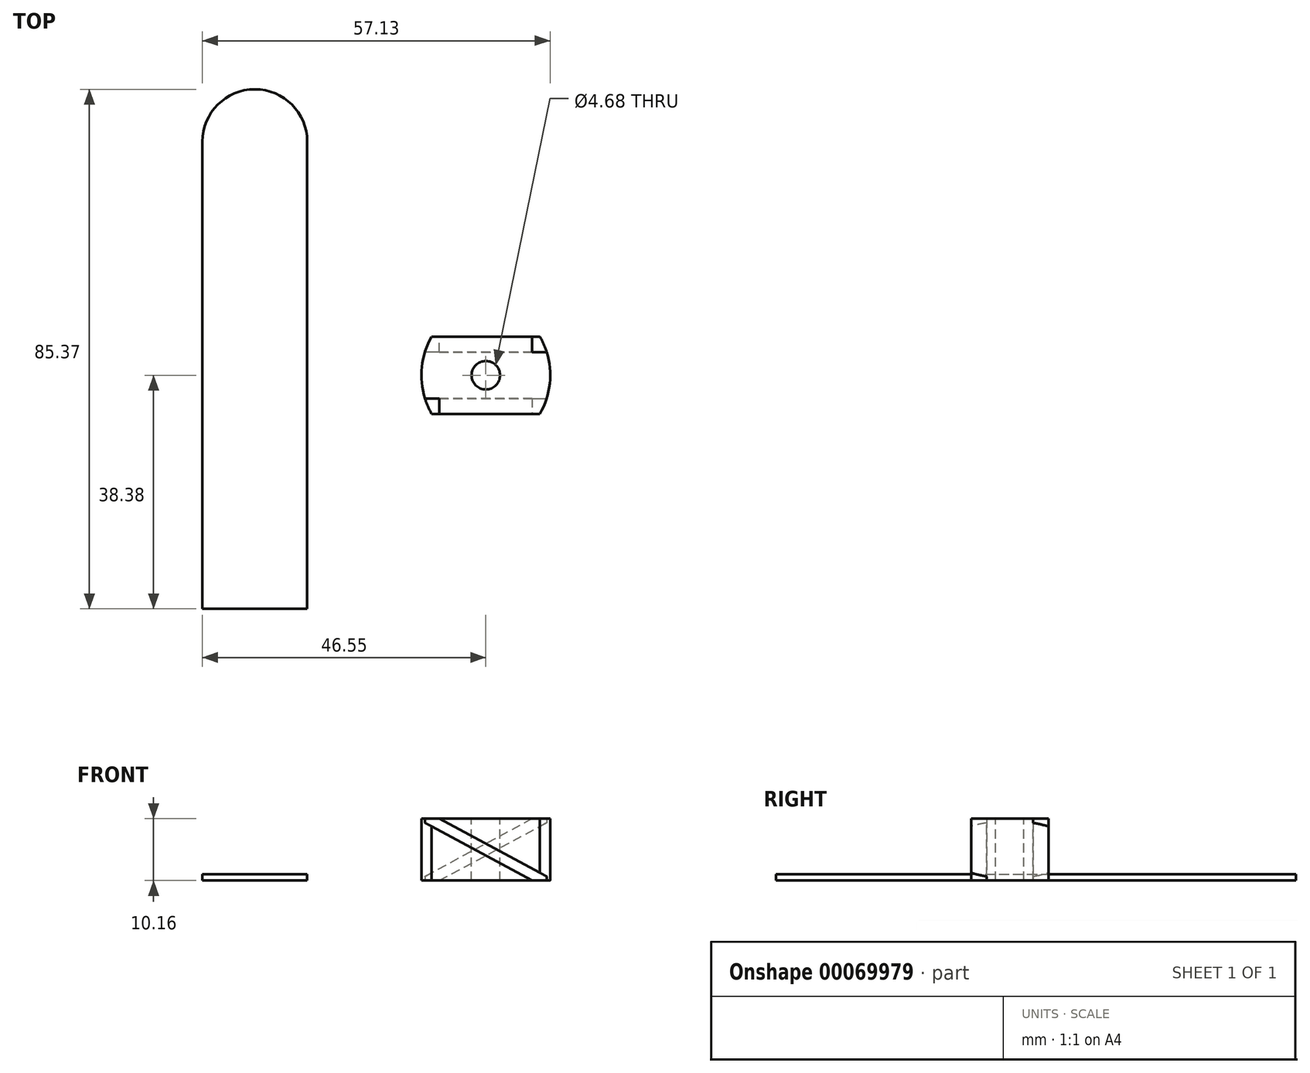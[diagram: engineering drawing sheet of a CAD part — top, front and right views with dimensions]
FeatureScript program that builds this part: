
annotation { "Feature Type Name" : "Feature", "Feature Type Description" : "" }
export const myFeature = defineFeature(function(context is Context, id is Id, definition is map)
    precondition{}
    {
        {
            var Q0;
            Q0=qCreatedBy(makeId("Top.planeOp"),FACE);
            var sketch = newSketch(context, id + "F0", { "sketchPlane" : qUnion([Q0])});
            skLineSegment(sketch, "E0.rect.bottom", {"start": v(-8.89, -6.35) * mm, "end": v(8.9, -6.35) * mm});
            skLineSegment(sketch, "E0.rect.top", {"start": v(-8.9, 6.35) * mm, "end": v(8.89, 6.35) * mm});
            skPoint(sketch, "E0.rect.middle", {"position": v(0, 0) * mm});
            skArc(sketch, "E1", {"start": v(-8.9, 6.35) * mm, "mid": v(-10.58, 0) * mm, "end": v(-8.89, -6.35) * mm});
            skLineSegment(sketch, "E2", {"start": v(0, 6.35) * mm, "end": v(0, -6.35) * mm});
            skArc(sketch, "E3.MirrorCS", {"start": v(8.9, 6.35) * mm, "mid": v(10.58, 0) * mm, "end": v(8.89, -6.35) * mm});
            skSolve(sketch);
        }
        {
            var Q0;
            Q0 = qSketchRegion(id + "F0", true);
            extrude(context, id + "F1", {"entities" : qUnion([Q0]), "depth" : 10.16 * mm});
        }
        {
            var Q0;
            Q0=makeQuery(id+"F1.opExtrude","SWEPT_FACE",FACE,{"disambiguationData":[OSD([sQuery(id+"F0.wireOp",EDGE,"E0.rect.bottom")])]});
            var sketch = newSketch(context, id + "F2", { "sketchPlane" : qUnion([Q0])});
            skPoint(sketch, "E4", {"position": v(8.89, 8.9) * mm});
            skPoint(sketch, "E5", {"position": v(7.62, 10.16) * mm});
            skPoint(sketch, "E6", {"position": v(8.89, 10.16) * mm});
            skPoint(sketch, "E7", {"position": v(-8.89, 0) * mm});
            skPoint(sketch, "E8", {"position": v(-8.89, 1.27) * mm});
            skPoint(sketch, "E9", {"position": v(-7.62, 0) * mm});
            skLineSegment(sketch, "E10", {"start": v(7.62, 10.16) * mm, "end": v(8.89, 10.16) * mm});
            skLineSegment(sketch, "E11", {"start": v(-7.62, 0) * mm, "end": v(-8.89, 0) * mm});
            skLineSegment(sketch, "E12", {"start": v(8.89, 10.16) * mm, "end": v(11.94, 10.16) * mm});
            skLineSegment(sketch, "E13", {"start": v(8.89, 8.9) * mm, "end": v(11.25, 10.16) * mm});
            skLineSegment(sketch, "E14.MirrorCS", {"start": v(8.89, 1.27) * mm, "end": v(-7.62, 10.16) * mm});
            skLineSegment(sketch, "E15.MirrorCS", {"start": v(7.62, 0) * mm, "end": v(-8.89, 8.9) * mm});
            skLineSegment(sketch, "E16.MirrorCS", {"start": v(-8.9, 10.16) * mm, "end": v(-11.94, 10.16) * mm});
            skLineSegment(sketch, "E17.MirrorCS", {"start": v(-8.89, 8.9) * mm, "end": v(-11.25, 10.16) * mm});
            skLineSegment(sketch, "E18.MirrorCS", {"start": v(-7.62, 10.16) * mm, "end": v(-8.89, 10.16) * mm});
            skLineSegment(sketch, "E19.MirrorCS", {"start": v(7.62, 0) * mm, "end": v(8.89, 0) * mm});
            skLineSegment(sketch, "E20.MirrorCS", {"start": v(8.89, 0) * mm, "end": v(11.88, 0) * mm});
            skLineSegment(sketch, "E21.MirrorCS", {"start": v(8.89, 1.27) * mm, "end": v(11.25, 0) * mm});
            skSolve(sketch);
        }
        {
            var Q0;
            Q0 = qSketchRegion(id + "F2", true);
            var Q1;
            {var subQ4=sQuery(id+"F2.wireOp",EDGE,"FS7OZLvG-7SUy-ogdl-wZkU-jxt60eXpT3zC");Q1=makeQuery(id+"F2.imprint","IMPRINT",FACE,{"disambiguationData":[TD([[makeQuery(id+"F2.imprint","IMPRINT",EDGE,{"derivedFrom":subQ4}),1.0]])]});}
            extrude(context, id + "F3", {"entities" : qUnion([Q0, Q1]), "operationType" : NewBodyOperationType.REMOVE, "oppositeDirection" : true, "depth" : 2.54 * mm});
        }
        {
            var Q0;
            Q0=makeQuery(id+"F1.opExtrude","SWEPT_FACE",FACE,{"disambiguationData":[OSD([sQuery(id+"F0.wireOp",EDGE,"E0.rect.top")])]});
            var sketch = newSketch(context, id + "F4", { "sketchPlane" : qUnion([Q0])});
            skPoint(sketch, "E22", {"position": v(-8.9, 0) * mm});
            skPoint(sketch, "E23", {"position": v(-7.62, 0) * mm});
            skPoint(sketch, "E24", {"position": v(-8.9, 1.27) * mm});
            skPoint(sketch, "E25", {"position": v(7.62, 10.16) * mm});
            skPoint(sketch, "E26", {"position": v(8.9, 8.9) * mm});
            skPoint(sketch, "E27", {"position": v(8.9, 10.16) * mm});
            skLineSegment(sketch, "E28", {"start": v(-7.62, 0) * mm, "end": v(-11.53, 0) * mm});
            skLineSegment(sketch, "E29", {"start": v(0, 10.16) * mm, "end": v(0, 0) * mm});
            skLineSegment(sketch, "E30.MirrorCS", {"start": v(-7.62, 10.16) * mm, "end": v(8.9, 1.27) * mm});
            skLineSegment(sketch, "E31.MirrorCS", {"start": v(7.62, 0) * mm, "end": v(-8.9, 8.9) * mm});
            skLineSegment(sketch, "E32.MirrorCS", {"start": v(8.9, 1.27) * mm, "end": v(11.25, 0) * mm});
            skLineSegment(sketch, "E33.MirrorCS", {"start": v(7.62, 0) * mm, "end": v(11.53, 0) * mm});
            skLineSegment(sketch, "E34.MirrorCS", {"start": v(-7.62, 10.16) * mm, "end": v(-12.9, 10.16) * mm});
            skLineSegment(sketch, "E35", {"start": v(-8.9, 8.9) * mm, "end": v(-11.25, 10.16) * mm});
            skSolve(sketch);
        }
        {
            var Q0;
            Q0 = qSketchRegion(id + "F4", true);
            extrude(context, id + "F5", {"entities" : qUnion([Q0]), "operationType" : NewBodyOperationType.REMOVE, "oppositeDirection" : true, "depth" : 2.54 * mm});
        }
        {
            var Q0;
            Q0=makeQuery(id+"F1.opExtrude","CAP_FACE",FACE,{"disambiguationData":[OSD([sQuery(id+"F0.wireOp",EDGE,"E0.rect.bottom"),sQuery(id+"F0.wireOp",EDGE,"E0.rect.top"),sQuery(id+"F0.wireOp",EDGE,"E1"),sQuery(id+"F0.wireOp",EDGE,"E3.MirrorCS")])],"isStart":false});
            var sketch = newSketch(context, id + "F6", { "sketchPlane" : qUnion([Q0])});
            skCircle(sketch, "E36", {"center": v(0, 0) * mm, "radius": 2.34 * mm});
            skSolve(sketch);
        }
        {
            var Q0;
            Q0 = qSketchRegion(id + "F6", true);
            extrude(context, id + "F7", {"entities" : qUnion([Q0]), "operationType" : NewBodyOperationType.REMOVE, "endBound" : BoundingType.THROUGH_ALL, "oppositeDirection" : true, "depth" : 25.4 * mm});
        }
        {
            var Q0;
            Q0=qCreatedBy(makeId("Top.planeOp"),FACE);
            var sketch = newSketch(context, id + "F8", { "sketchPlane" : qUnion([Q0])});
            skLineSegment(sketch, "E37.rect.bottom", {"start": v(-46.55, -38.38) * mm, "end": v(-29.33, -38.38) * mm});
            skLineSegment(sketch, "E37.rect.left", {"start": v(-46.55, -38.38) * mm, "end": v(-46.55, 38.38) * mm});
            skLineSegment(sketch, "E37.rect.right", {"start": v(-29.33, -38.38) * mm, "end": v(-29.33, 38.38) * mm});
            skPoint(sketch, "E37.rect.middle", {"position": v(-37.94, 0) * mm});
            skArc(sketch, "E38", {"start": v(-29.33, 38.38) * mm, "mid": v(-37.94, 46.99) * mm, "end": v(-46.55, 38.38) * mm});
            skSolve(sketch);
        }
        {
            var Q0;
            Q0 = qSketchRegion(id + "F8", true);
            extrude(context, id + "F9", {"entities" : qUnion([Q0]), "depth" : 1.02 * mm});
        }
    });
